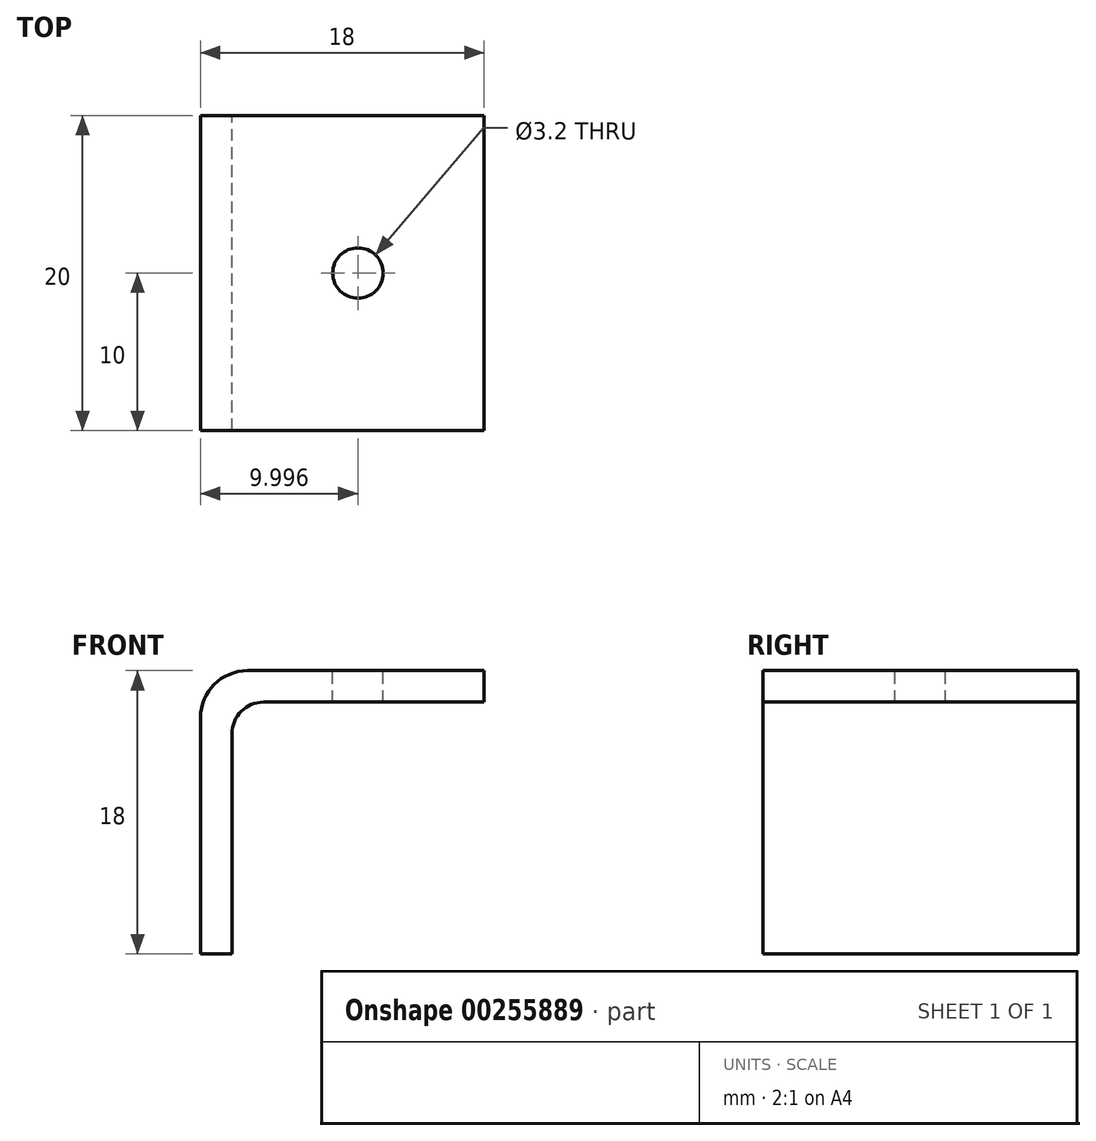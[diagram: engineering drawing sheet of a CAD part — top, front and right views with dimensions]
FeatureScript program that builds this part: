
annotation { "Feature Type Name" : "Feature", "Feature Type Description" : "" }
export const myFeature = defineFeature(function(context is Context, id is Id, definition is map)
    precondition{}
    {
        {
            var Q0;
            Q0=qCreatedBy(makeId("Front.planeOp"),FACE);
            var sketch = newSketch(context, id + "F0", { "sketchPlane" : qUnion([Q0])});
            skLineSegment(sketch, "E0", {"start": v(-24.05, -16.97) * mm, "end": v(-24.05, 1.03) * mm});
            skLineSegment(sketch, "E1", {"start": v(-24.05, 1.03) * mm, "end": v(-6.05, 1.03) * mm});
            skLineSegment(sketch, "E2", {"start": v(-6.05, 1.03) * mm, "end": v(-6.05, -0.97) * mm});
            skLineSegment(sketch, "E3", {"start": v(-6.05, -0.97) * mm, "end": v(-22.05, -0.97) * mm});
            skLineSegment(sketch, "E4", {"start": v(-22.05, -0.97) * mm, "end": v(-22.05, -16.97) * mm});
            skLineSegment(sketch, "E5", {"start": v(-22.05, -16.97) * mm, "end": v(-24.05, -16.97) * mm});
            skSolve(sketch);
        }
        {
            var Q0;
            Q0=makeQuery(id+"F0.imprint","IMPRINT",FACE,{"disambiguationData":[TD([[makeQuery(id+"F0.imprint","IMPRINT",EDGE,{"derivedFrom":sQuery(id+"F0.wireOp",EDGE,"E0")}),-1.0]])]});
            extrude(context, id + "F1", {"entities" : qUnion([Q0]), "depth" : 20 * mm});
        }
        {
            var Q0;
            Q0=makeQuery(id+"F1.opExtrude","SWEPT_FACE",FACE,{"disambiguationData":[OSD([sQuery(id+"F0.wireOp",EDGE,"E1")])]});
            var sketch = newSketch(context, id + "F2", { "sketchPlane" : qUnion([Q0])});
            skPoint(sketch, "E6", {"position": v(-14.05, -10) * mm});
            skLineSegment(sketch, "E7", {"start": v(-22.05, 0) * mm, "end": v(-22.05, -20) * mm, "construction": true});
            skLineSegment(sketch, "E8", {"start": v(-22.05, 0) * mm, "end": v(-6.05, -20) * mm, "construction": true});
            skSolve(sketch);
        }
        {
            var Q0;
            Q0=sQuery(id+"F2.wireOp",VERTEX,"E6");
            var Q1;
            Q1=makeQuery(id+"F1.opExtrude","SWEPT_BODY",BODY,{"disambiguationData":[OSD([sQuery(id+"F0.wireOp",EDGE,"E0"),sQuery(id+"F0.wireOp",EDGE,"E1"),sQuery(id+"F0.wireOp",EDGE,"E2"),sQuery(id+"F0.wireOp",EDGE,"E3"),sQuery(id+"F0.wireOp",EDGE,"E4"),sQuery(id+"F0.wireOp",EDGE,"E5")])]});
            hole(context, id + "F3", {"style" : HoleStyle.SIMPLE, "endStyle" : HoleEndStyle.THROUGH, "standardTappedOrClearance" : lookupTablePath({ "standard" : "ISO", "engagement" : "75%", "pitch" : "0.75 mm", "size" : "M4", "type" : "Tapped" }), "standardBlindInLast" : lookupTablePath({ "standard" : "ISO", "engagement" : "75%", "pitch" : "0.75 mm", "size" : "M4", "type" : "Tapped" }), "holeDiameter" : 3.2 * mm, "showTappedDepth" : true, "tappedDepth" : 12 * mm, "tapClearance" : 3, "startFromSketch" : true, "locations" : qUnion([Q0]), "scope" : qUnion([Q1])});
        }
        {
            var Q0;
            Q0=makeQuery(id+"F1.opExtrude","SWEPT_EDGE",EDGE,{"disambiguationData":[OSD([sQuery(id+"F0.wireOp",EDGE,"E0"),sQuery(id+"F0.wireOp",EDGE,"E1")])]});
            fillet(context, id + "F4", {"entities" : qUnion([Q0]), "radius" : 3 * mm, "tangentPropagation" : true, "allowEdgeOverflow" : false});
        }
        {
            var Q0;
            Q0=makeQuery(id+"F1.opExtrude","SWEPT_EDGE",EDGE,{"disambiguationData":[OSD([sQuery(id+"F0.wireOp",EDGE,"E3"),sQuery(id+"F0.wireOp",EDGE,"E4")])]});
            fillet(context, id + "F5", {"entities" : qUnion([Q0]), "radius" : 2 * mm, "tangentPropagation" : true, "allowEdgeOverflow" : false});
        }
    });
